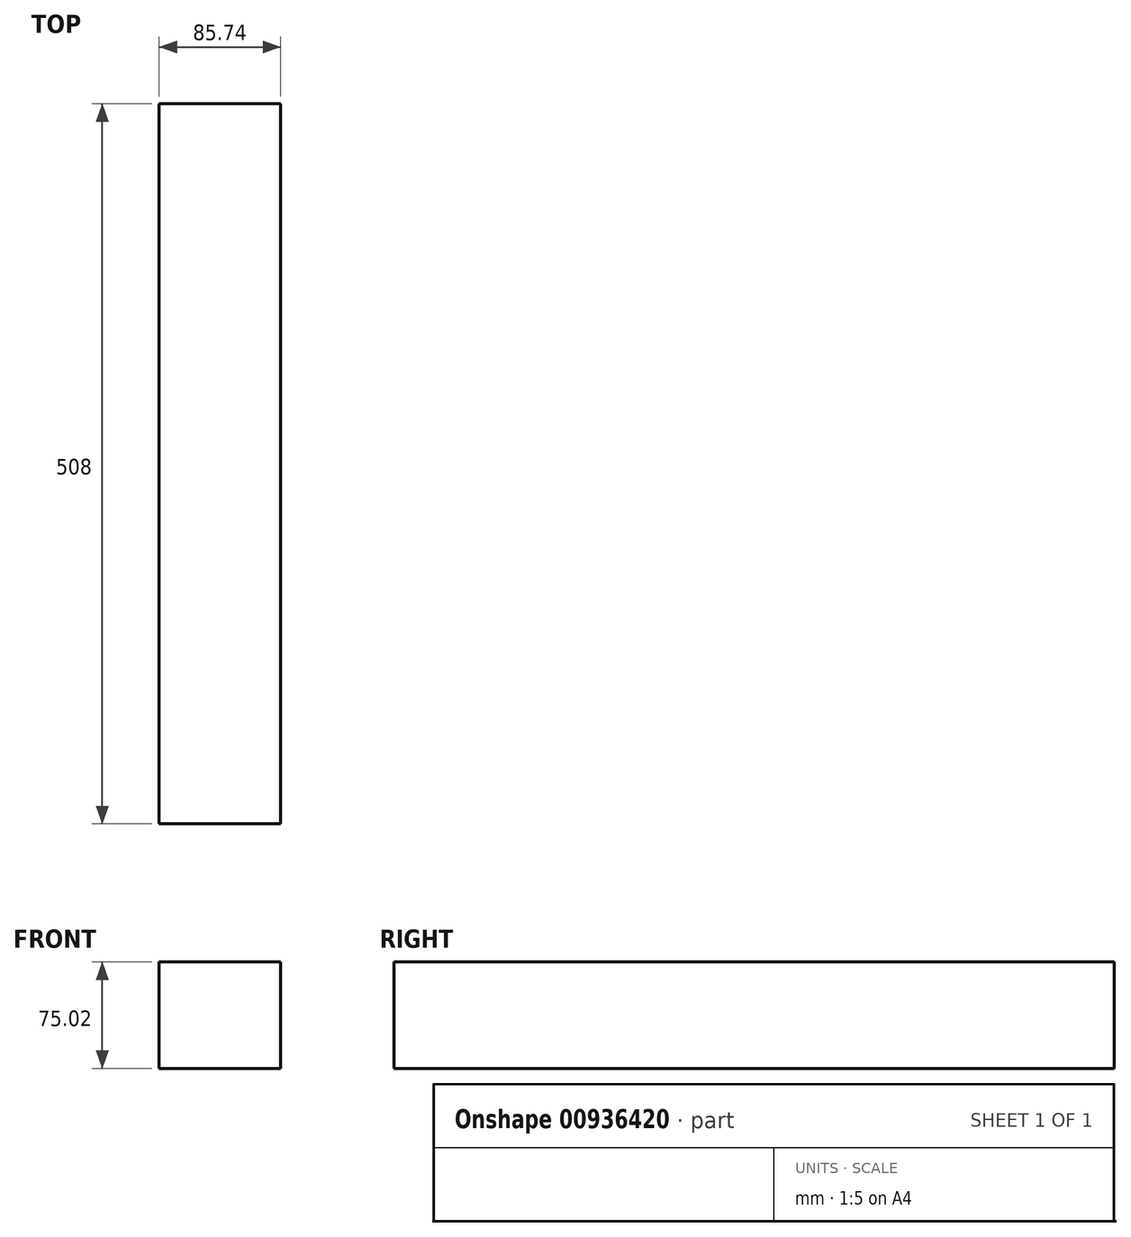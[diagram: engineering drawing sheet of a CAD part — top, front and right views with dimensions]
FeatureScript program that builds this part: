
annotation { "Feature Type Name" : "Feature", "Feature Type Description" : "" }
export const myFeature = defineFeature(function(context is Context, id is Id, definition is map)
    precondition{}
    {
        {
            var Q0;
            Q0=qCreatedBy(makeId("Front.planeOp"),FACE);
            var sketch = newSketch(context, id + "F0", { "sketchPlane" : qUnion([Q0])});
            skLineSegment(sketch, "E0.bottom", {"start": v(-40.65, 28.09) * mm, "end": v(45.09, 28.09) * mm});
            skLineSegment(sketch, "E0.top", {"start": v(-40.65, -46.93) * mm, "end": v(45.09, -46.93) * mm});
            skLineSegment(sketch, "E0.left", {"start": v(-40.65, 28.09) * mm, "end": v(-40.65, -46.93) * mm});
            skLineSegment(sketch, "E0.right", {"start": v(45.09, 28.09) * mm, "end": v(45.09, -46.93) * mm});
            skSolve(sketch);
        }
        {
            var Q0;
            Q0=makeQuery(id+"F0.imprint","IMPRINT",FACE,{"disambiguationData":[TD([[makeQuery(id+"F0.imprint","IMPRINT",EDGE,{"derivedFrom":sQuery(id+"F0.wireOp",EDGE,"E0.bottom")}),-1.0]])]});
            extrude(context, id + "F1", {"entities" : qUnion([Q0]), "depth" : 508 * mm, "offsetDistance" : 25.4 * mm});
        }
    });
